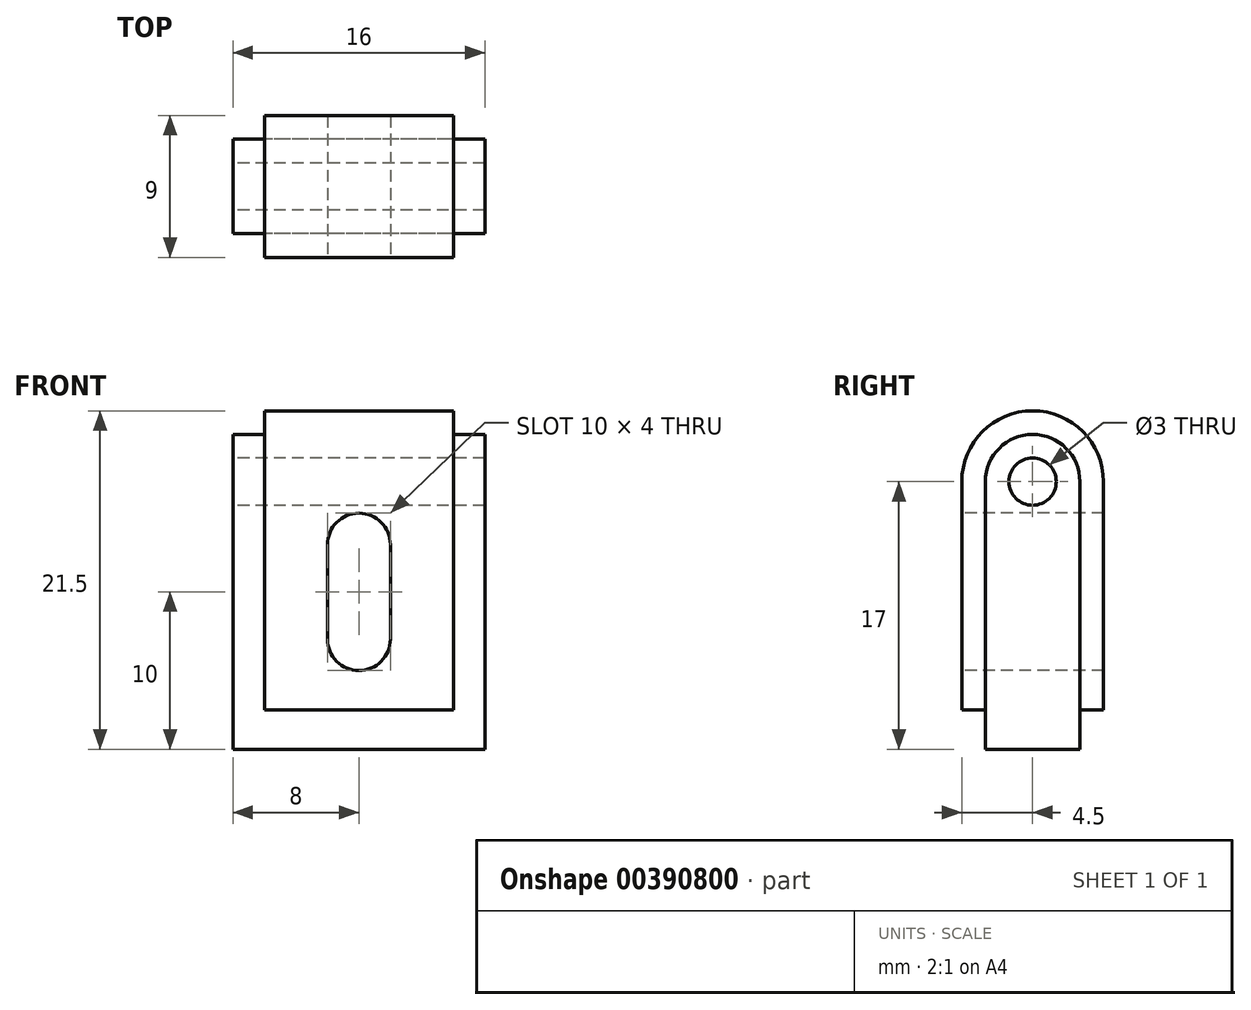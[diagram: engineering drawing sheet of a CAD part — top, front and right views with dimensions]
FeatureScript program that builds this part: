
annotation { "Feature Type Name" : "Feature", "Feature Type Description" : "" }
export const myFeature = defineFeature(function(context is Context, id is Id, definition is map)
    precondition{}
    {
        {
            var Q0;
            Q0=qCreatedBy(makeId("Right.planeOp"),FACE);
            var sketch = newSketch(context, id + "F0", { "sketchPlane" : qUnion([Q0])});
            skLineSegment(sketch, "E0.bottom", {"start": v(3, -10) * mm, "end": v(-3, -10) * mm});
            skLineSegment(sketch, "E0.top", {"start": v(0, 10) * mm, "end": v(0, 10) * mm});
            skLineSegment(sketch, "E0.left", {"start": v(3, -10) * mm, "end": v(3, 7) * mm});
            skLineSegment(sketch, "E0.right", {"start": v(-3, -10) * mm, "end": v(-3, 7) * mm});
            skPoint(sketch, "E0.middle", {"position": v(0, 0) * mm});
            skPoint(sketch, "E1.visualSharp", {"position": v(-3, 10) * mm});
            skArc(sketch, "E1.filletArc", {"start": v(0, 10) * mm, "mid": v(-2.12, 9.12) * mm, "end": v(-3, 7) * mm});
            skPoint(sketch, "E2.visualSharp", {"position": v(3, 10) * mm});
            skArc(sketch, "E2.filletArc", {"start": v(3, 7) * mm, "mid": v(2.12, 9.12) * mm, "end": v(0, 10) * mm});
            skArc(sketch, "E3.0", {"start": v(0, 11.5) * mm, "mid": v(-3.18, 10.18) * mm, "end": v(-4.5, 7) * mm});
            skArc(sketch, "E3.1", {"start": v(4.5, 7) * mm, "mid": v(3.18, 10.18) * mm, "end": v(0, 11.5) * mm});
            skLineSegment(sketch, "E4", {"start": v(-4.5, 7) * mm, "end": v(-4.5, -7.49) * mm});
            skLineSegment(sketch, "E5", {"start": v(-4.5, -7.49) * mm, "end": v(-3, -7.49) * mm});
            skLineSegment(sketch, "E6.MirrorCS", {"start": v(4.5, 7) * mm, "end": v(4.5, -7.49) * mm});
            skLineSegment(sketch, "E7.MirrorCS", {"start": v(4.5, -7.49) * mm, "end": v(3, -7.49) * mm});
            skCircle(sketch, "E8", {"center": v(0, 7) * mm, "radius": 1.5 * mm});
            skSolve(sketch);
        }
        {
            var Q0;
            {var subQ1=sQuery(id+"F0.wireOp",EDGE,"E0.bottom");Q0=makeQuery(id+"F0.imprint","IMPRINT",FACE,{"disambiguationData":[TD([[makeQuery(id+"F0.imprint","IMPRINT",EDGE,{"derivedFrom":subQ1}),-1.0]])]});}
            extrude(context, id + "F1", {"entities" : qUnion([Q0]), "depth" : 8 * mm, "hasSecondDirection" : true, "secondDirectionOppositeDirection" : true, "secondDirectionDepth" : 8 * mm});
        }
        {
            var Q0;
            {var subQ1=sQuery(id+"F0.wireOp",EDGE,"E1.filletArc");Q0=makeQuery(id+"F0.imprint","IMPRINT",FACE,{"disambiguationData":[TD([[makeQuery(id+"F0.imprint","IMPRINT",EDGE,{"derivedFrom":subQ1}),-1.0]])]});}
            extrude(context, id + "F2", {"entities" : qUnion([Q0]), "operationType" : NewBodyOperationType.ADD, "depth" : 6 * mm, "hasSecondDirection" : true, "secondDirectionOppositeDirection" : true, "secondDirectionDepth" : 6 * mm});
        }
        {
            var Q0;
            Q0=makeQuery(id+"F2.opExtrude","SWEPT_FACE",FACE,{"disambiguationData":[OSD([sQuery(id+"F0.wireOp",EDGE,"E4")])]});
            var sketch = newSketch(context, id + "F3", { "sketchPlane" : qUnion([Q0])});
            skLineSegment(sketch, "E9.bottom", {"start": v(0, 5) * mm, "end": v(0, 5) * mm});
            skLineSegment(sketch, "E9.top", {"start": v(0, -5) * mm, "end": v(0, -5) * mm});
            skLineSegment(sketch, "E9.left", {"start": v(2, 3) * mm, "end": v(2, -3) * mm});
            skLineSegment(sketch, "E9.right", {"start": v(-2, 3) * mm, "end": v(-2, -3) * mm});
            skPoint(sketch, "E9.middle", {"position": v(0, 0) * mm});
            skPoint(sketch, "E10.visualSharp", {"position": v(-2, 5) * mm});
            skArc(sketch, "E10.filletArc", {"start": v(0, 5) * mm, "mid": v(-1.41, 4.41) * mm, "end": v(-2, 3) * mm});
            skPoint(sketch, "E11.visualSharp", {"position": v(2, 5) * mm});
            skArc(sketch, "E11.filletArc", {"start": v(2, 3) * mm, "mid": v(1.41, 4.41) * mm, "end": v(0, 5) * mm});
            skPoint(sketch, "E12.visualSharp", {"position": v(2, -5) * mm});
            skArc(sketch, "E12.filletArc", {"start": v(0, -5) * mm, "mid": v(1.41, -4.41) * mm, "end": v(2, -3) * mm});
            skPoint(sketch, "E13.visualSharp", {"position": v(-2, -5) * mm});
            skArc(sketch, "E13.filletArc", {"start": v(-2, -3) * mm, "mid": v(-1.41, -4.41) * mm, "end": v(0, -5) * mm});
            skSolve(sketch);
        }
        {
            var Q0;
            Q0=makeQuery(id+"F3.imprint","IMPRINT",FACE,{"disambiguationData":[TD([[makeQuery(id+"F3.imprint","IMPRINT",EDGE,{"derivedFrom":sQuery(id+"F3.wireOp",EDGE,"E9.left")}),-1.0]])]});
            extrude(context, id + "F4", {"entities" : qUnion([Q0]), "operationType" : NewBodyOperationType.REMOVE, "oppositeDirection" : true, "depth" : 25 * mm});
        }
    });
